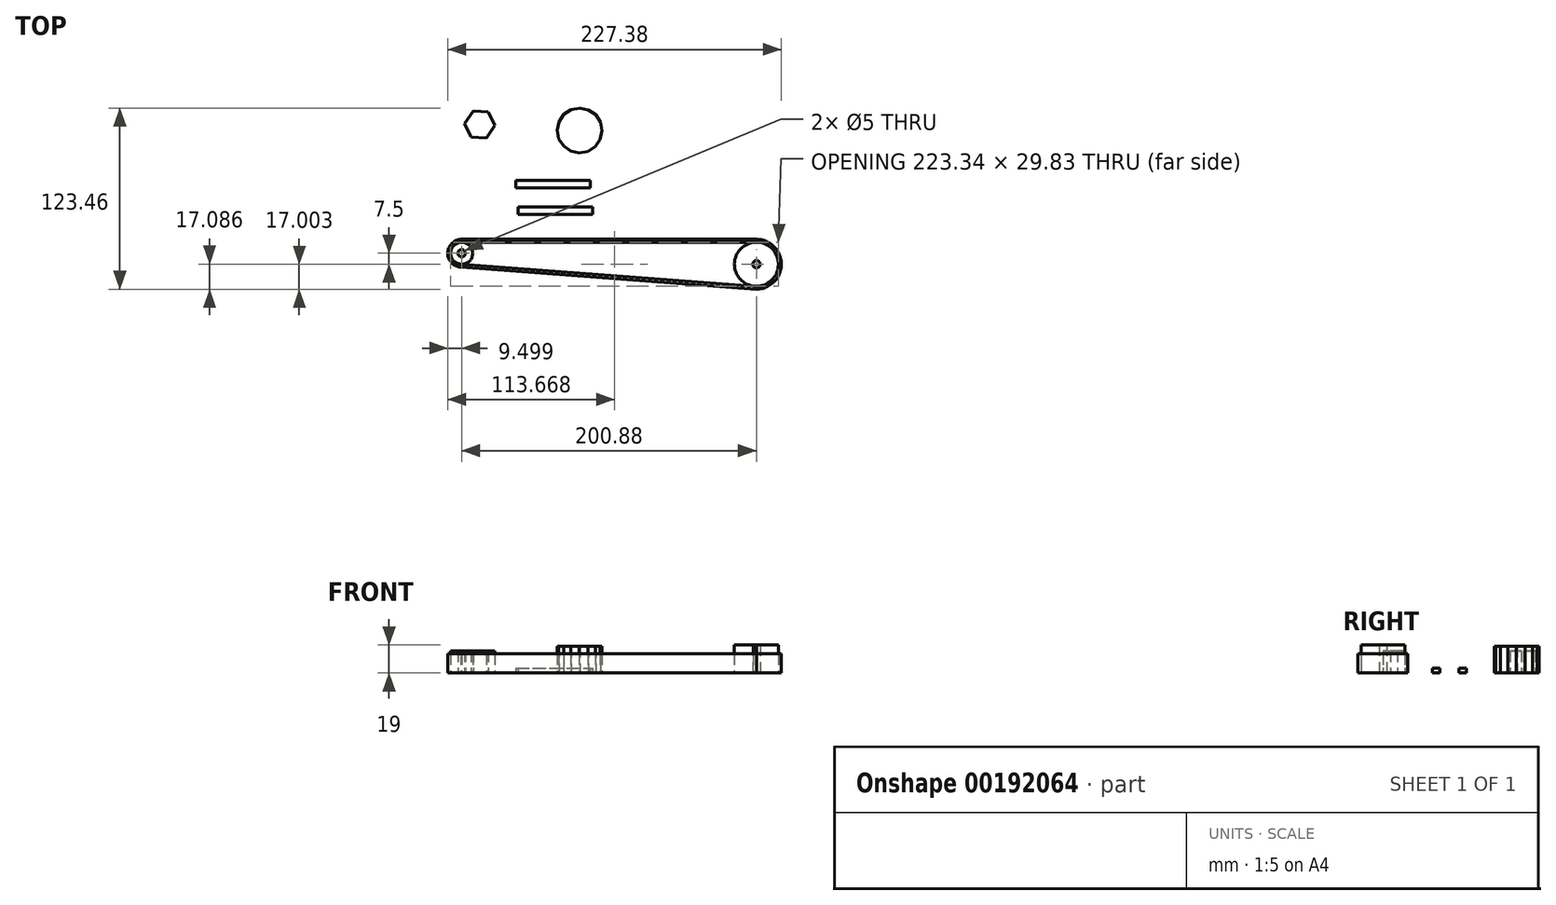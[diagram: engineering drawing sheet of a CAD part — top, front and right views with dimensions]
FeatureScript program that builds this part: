
annotation { "Feature Type Name" : "Feature", "Feature Type Description" : "" }
export const myFeature = defineFeature(function(context is Context, id is Id, definition is map)
    precondition{}
    {
        {
            var Q0;
            Q0=qCreatedBy(makeId("Top.planeOp"),FACE);
            var sketch = newSketch(context, id + "F0", { "sketchPlane" : qUnion([Q0])});
            skLineSegment(sketch, "E0.bottom", {"start": v(-25.4, 2.54) * mm, "end": v(25.4, 2.54) * mm});
            skLineSegment(sketch, "E0.top", {"start": v(-25.4, -2.54) * mm, "end": v(25.4, -2.54) * mm});
            skLineSegment(sketch, "E0.left", {"start": v(-25.4, 2.54) * mm, "end": v(-25.4, -2.54) * mm});
            skLineSegment(sketch, "E0.right", {"start": v(25.4, 2.54) * mm, "end": v(25.4, -2.54) * mm});
            skPoint(sketch, "E0.middle", {"position": v(0, 0) * mm});
            skLineSegment(sketch, "E1.bottom", {"start": v(-26.97, 20.7) * mm, "end": v(23.83, 20.7) * mm});
            skLineSegment(sketch, "E1.top", {"start": v(-26.97, 15.61) * mm, "end": v(23.83, 15.61) * mm});
            skLineSegment(sketch, "E1.left", {"start": v(-26.97, 20.7) * mm, "end": v(-26.97, 15.61) * mm});
            skLineSegment(sketch, "E1.right", {"start": v(23.83, 20.7) * mm, "end": v(23.83, 15.61) * mm});
            skPoint(sketch, "E1.middle", {"position": v(-1.57, 18.15) * mm});
            skSolve(sketch);
        }
        {
            var Q0;
            Q0=makeQuery(id+"F0.imprint","IMPRINT",FACE,{"disambiguationData":[TD([[makeQuery(id+"F0.imprint","IMPRINT",EDGE,{"derivedFrom":sQuery(id+"F0.wireOp",EDGE,"E0.bottom")}),-1.0]])]});
            var Q1;
            Q1=makeQuery(id+"F0.imprint","IMPRINT",FACE,{"disambiguationData":[TD([[makeQuery(id+"F0.imprint","IMPRINT",EDGE,{"derivedFrom":sQuery(id+"F0.wireOp",EDGE,"E1.bottom")}),-1.0]])]});
            extrude(context, id + "F1", {"entities" : qUnion([Q0, Q1]), "depth" : 3.17 * mm});
        }
        {
            var Q0;
            Q0=qCreatedBy(makeId("Top.planeOp"),FACE);
            var sketch = newSketch(context, id + "F2", { "sketchPlane" : qUnion([Q0])});
            skCircle(sketch, "E2", {"center": v(-63.82, -28.85) * mm, "radius": 7.5 * mm});
            skCircle(sketch, "E3", {"center": v(137.06, -36.35) * mm, "radius": 15 * mm});
            skLineSegment(sketch, "E4", {"start": v(-63.82, -21.35) * mm, "end": v(137.06, -21.35) * mm});
            skLineSegment(sketch, "E5", {"start": v(137.06, -51.35) * mm, "end": v(-63.82, -36.37) * mm});
            skLineSegment(sketch, "E6", {"start": v(-63.82, -21.35) * mm, "end": v(-63.82, -36.37) * mm});
            skLineSegment(sketch, "E7", {"start": v(137.06, -21.35) * mm, "end": v(137.06, -51.35) * mm});
            skCircle(sketch, "E8", {"center": v(-63.82, -28.85) * mm, "radius": 2.5 * mm});
            skCircle(sketch, "E9", {"center": v(137.06, -36.35) * mm, "radius": 2.5 * mm});
            skCircle(sketch, "E10", {"center": v(-63.82, -28.85) * mm, "radius": 9.5 * mm});
            skCircle(sketch, "E11", {"center": v(137.06, -36.35) * mm, "radius": 17 * mm});
            skLineSegment(sketch, "E12", {"start": v(-64.31, -19.36) * mm, "end": v(137.06, -19.35) * mm});
            skLineSegment(sketch, "E13", {"start": v(137.06, -53.35) * mm, "end": v(-64.53, -38.32) * mm});
            skSolve(sketch);
        }
        {
            var Q0;
            {var subQ0=sQuery(id+"F2.wireOp",EDGE,"E6");var subQ1=sQuery(id+"F2.wireOp",EDGE,"E2");var subQ3=makeQuery(id+"F2.imprint","INTERSECT",VERTEX,{"derivedFrom":[subQ1,subQ0]});Q0=makeQuery(id+"F2.imprint","IMPRINT",FACE,{"disambiguationData":[TD([[makeQuery(id+"F2.imprint","IMPRINT",EDGE,{"disambiguationData":[TD([[subQ3,1.0]])],"derivedFrom":subQ0}),1.0]])]});}
            var Q1;
            {var subQ0=sQuery(id+"F2.wireOp",EDGE,"E6");var subQ1=sQuery(id+"F2.wireOp",EDGE,"E2");var subQ3=makeQuery(id+"F2.imprint","INTERSECT",VERTEX,{"derivedFrom":[subQ1,subQ0]});Q1=makeQuery(id+"F2.imprint","IMPRINT",FACE,{"disambiguationData":[TD([[makeQuery(id+"F2.imprint","IMPRINT",EDGE,{"disambiguationData":[TD([[subQ3,1.0]])],"derivedFrom":subQ0}),-1.0]])]});}
            extrude(context, id + "F3", {"entities" : qUnion([Q0, Q1]), "depth" : 15 * mm});
        }
        {
            var Q0;
            {var subQ0=sQuery(id+"F2.wireOp",EDGE,"E7");var subQ4=sQuery(id+"F2.wireOp",EDGE,"E9");var subQ5=makeQuery(id+"F2.imprint","INTERSECT",VERTEX,{"disambiguationData":[OD(0.0)],"derivedFrom":[subQ0,subQ4]});Q0=makeQuery(id+"F2.imprint","IMPRINT",FACE,{"disambiguationData":[TD([[makeQuery(id+"F2.imprint","IMPRINT",EDGE,{"disambiguationData":[TD([[subQ5,1.0]])],"derivedFrom":subQ4}),-1.0]])]});}
            var Q1;
            {var subQ0=sQuery(id+"F2.wireOp",EDGE,"E7");var subQ4=sQuery(id+"F2.wireOp",EDGE,"E9");var subQ7=makeQuery(id+"F2.imprint","INTERSECT",VERTEX,{"disambiguationData":[OD(0.0)],"derivedFrom":[subQ0,subQ4]});Q1=makeQuery(id+"F2.imprint","IMPRINT",FACE,{"disambiguationData":[TD([[makeQuery(id+"F2.imprint","IMPRINT",EDGE,{"disambiguationData":[TD([[subQ7,-1.0]])],"derivedFrom":subQ4}),-1.0]])]});}
            extrude(context, id + "F4", {"entities" : qUnion([Q0, Q1]), "depth" : 19 * mm});
        }
        {
            var Q0;
            {var subQ2=sQuery(id+"F2.wireOp",EDGE,"E3");var subQ6=sQuery(id+"F2.wireOp",EDGE,"E5");var subQ8=makeQuery(id+"F2.imprint","INTERSECT",VERTEX,{"derivedFrom":[subQ2,subQ6]});Q0=makeQuery(id+"F2.imprint","IMPRINT",FACE,{"disambiguationData":[TD([[makeQuery(id+"F2.imprint","IMPRINT",EDGE,{"disambiguationData":[TD([[subQ8,-1.0]])],"derivedFrom":subQ6}),1.0]])]});}
            var Q1;
            {var subQ0=sQuery(id+"F2.wireOp",EDGE,"E10");var subQ1=sQuery(id+"F2.wireOp",EDGE,"E4");var subQ2=makeQuery(id+"F2.imprint","INTERSECT",VERTEX,{"derivedFrom":[subQ1,subQ0]});Q1=makeQuery(id+"F2.imprint","IMPRINT",FACE,{"disambiguationData":[TD([[makeQuery(id+"F2.imprint","IMPRINT",EDGE,{"disambiguationData":[TD([[subQ2,-1.0]])],"derivedFrom":subQ1}),1.0]])]});}
            var Q2;
            {var subQ0=sQuery(id+"F2.wireOp",EDGE,"E11");var subQ1=sQuery(id+"F2.wireOp",EDGE,"E5");var subQ2=makeQuery(id+"F2.imprint","INTERSECT",VERTEX,{"derivedFrom":[subQ1,subQ0]});Q2=makeQuery(id+"F2.imprint","IMPRINT",FACE,{"disambiguationData":[TD([[makeQuery(id+"F2.imprint","IMPRINT",EDGE,{"disambiguationData":[TD([[subQ2,-1.0]])],"derivedFrom":subQ1}),1.0]])]});}
            var Q3;
            {var subQ0=sQuery(id+"F2.wireOp",EDGE,"E6");var subQ1=sQuery(id+"F2.wireOp",EDGE,"E5");var subQ2=makeQuery(id+"F2.imprint","INTERSECT",VERTEX,{"derivedFrom":[subQ1,subQ0]});Q3=makeQuery(id+"F2.imprint","IMPRINT",FACE,{"disambiguationData":[TD([[makeQuery(id+"F2.imprint","IMPRINT",EDGE,{"disambiguationData":[TD([[subQ2,1.0]])],"derivedFrom":subQ1}),1.0]])]});}
            extrude(context, id + "F5", {"entities" : qUnion([Q0, Q1, Q2, Q3]), "depth" : 13 * mm});
        }
        {
            var Q0;
            Q0=qCreatedBy(makeId("Top.planeOp"),FACE);
            var sketch = newSketch(context, id + "F6", { "sketchPlane" : qUnion([Q0])});
            skCircle(sketch, "E14.cCircle", {"center": v(-51.5, 58.9) * mm, "radius": 9 * mm, "construction": true});
            skLineSegment(sketch, "E14.0", {"start": v(-41.13, 58.16) * mm, "end": v(-46.95, 49.55) * mm});
            skLineSegment(sketch, "E14.1", {"start": v(-46.95, 49.55) * mm, "end": v(-57.32, 50.3) * mm});
            skLineSegment(sketch, "E14.2", {"start": v(-57.32, 50.3) * mm, "end": v(-61.86, 59.65) * mm});
            skLineSegment(sketch, "E14.3", {"start": v(-61.86, 59.65) * mm, "end": v(-56.03, 68.25) * mm});
            skLineSegment(sketch, "E14.4", {"start": v(-56.03, 68.25) * mm, "end": v(-45.66, 67.5) * mm});
            skLineSegment(sketch, "E14.5", {"start": v(-45.66, 67.5) * mm, "end": v(-41.13, 58.16) * mm});
            skPoint(sketch, "E14.0.midPoint", {"position": v(-44.04, 53.85) * mm});
            skCircle(sketch, "E15.cCircle", {"center": v(16.57, 54.81) * mm, "radius": 15 * mm, "construction": true});
            skLineSegment(sketch, "E15.0", {"start": v(30.62, 48.78) * mm, "end": v(27.24, 43.86) * mm});
            skLineSegment(sketch, "E15.1", {"start": v(27.24, 43.86) * mm, "end": v(22.23, 40.6) * mm});
            skLineSegment(sketch, "E15.2", {"start": v(22.23, 40.6) * mm, "end": v(16.36, 39.52) * mm});
            skLineSegment(sketch, "E15.3", {"start": v(16.36, 39.52) * mm, "end": v(10.53, 40.76) * mm});
            skLineSegment(sketch, "E15.4", {"start": v(10.53, 40.76) * mm, "end": v(5.6, 44.14) * mm});
            skLineSegment(sketch, "E15.5", {"start": v(5.6, 44.14) * mm, "end": v(2.36, 49.15) * mm});
            skLineSegment(sketch, "E15.6", {"start": v(2.36, 49.15) * mm, "end": v(1.27, 55.02) * mm});
            skLineSegment(sketch, "E15.7", {"start": v(1.27, 55.02) * mm, "end": v(2.52, 60.85) * mm});
            skLineSegment(sketch, "E15.8", {"start": v(2.52, 60.85) * mm, "end": v(5.9, 65.77) * mm});
            skLineSegment(sketch, "E15.9", {"start": v(5.9, 65.77) * mm, "end": v(10.9, 69.02) * mm});
            skLineSegment(sketch, "E15.10", {"start": v(10.9, 69.02) * mm, "end": v(16.77, 70.1) * mm});
            skLineSegment(sketch, "E15.11", {"start": v(16.77, 70.1) * mm, "end": v(22.6, 68.87) * mm});
            skLineSegment(sketch, "E15.12", {"start": v(22.6, 68.87) * mm, "end": v(27.52, 65.48) * mm});
            skLineSegment(sketch, "E15.13", {"start": v(27.52, 65.48) * mm, "end": v(30.77, 60.48) * mm});
            skLineSegment(sketch, "E15.14", {"start": v(30.77, 60.48) * mm, "end": v(31.86, 54.61) * mm});
            skLineSegment(sketch, "E15.15", {"start": v(31.86, 54.61) * mm, "end": v(30.62, 48.78) * mm});
            skPoint(sketch, "E15.0.midPoint", {"position": v(28.93, 46.32) * mm});
            skSolve(sketch);
        }
        {
            var Q0;
            Q0=makeQuery(id+"F6.imprint","IMPRINT",FACE,{"disambiguationData":[TD([[makeQuery(id+"F6.imprint","IMPRINT",EDGE,{"derivedFrom":sQuery(id+"F6.wireOp",EDGE,"E14.0")}),-1.0]])]});
            extrude(context, id + "F7", {"entities" : qUnion([Q0]), "depth" : 15 * mm});
        }
        {
            var Q0;
            Q0=makeQuery(id+"F6.imprint","IMPRINT",FACE,{"disambiguationData":[TD([[makeQuery(id+"F6.imprint","IMPRINT",EDGE,{"derivedFrom":sQuery(id+"F6.wireOp",EDGE,"E15.0")}),-1.0]])]});
            extrude(context, id + "F8", {"entities" : qUnion([Q0]), "depth" : 18 * mm});
        }
    });
